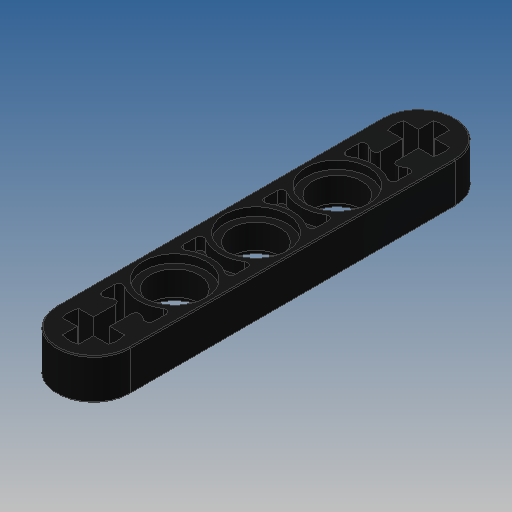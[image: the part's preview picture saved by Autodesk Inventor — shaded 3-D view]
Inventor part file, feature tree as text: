
AUTODESK INVENTOR PART (.ipt)
format: ipt  version: 2022.2 (Build 262287000, 287)  size: 283,648 bytes
history: native  units: mm
features: extrude x3, sketch x2, mirror x1, fillet x1
ambient origin geometry x8: Origin, YZ Plane, XZ Plane, XY Plane, X Axis, Y Axis, Z Axis, Center Point
bodies: Solid1 (feature_tree)
feature tree (7):
  sketch  "Sketch1"  dims[d8=4.8mm d9=6.4mm]
  extrude  "Extrusion1"  Depth=6.4mm
  extrude  "Extrusion9"  Depth=7.2mm
  extrude  "Extrusion7"  Depth=8.0mm
  mirror  "Mirror1"
  fillet  "Fillet1"  Radius=0.8mm
  sketch  "Sketch6"  dims[d14=4.0mm d15=0.0mm d32=7.2mm d34=8.0mm d41=0.8mm d42=0.0mm d45=0.1mm d46=0.4mm d52=1.6mm d53=6.2mm d54=45.0deg d55=1.6mm d56=0.0mm]
